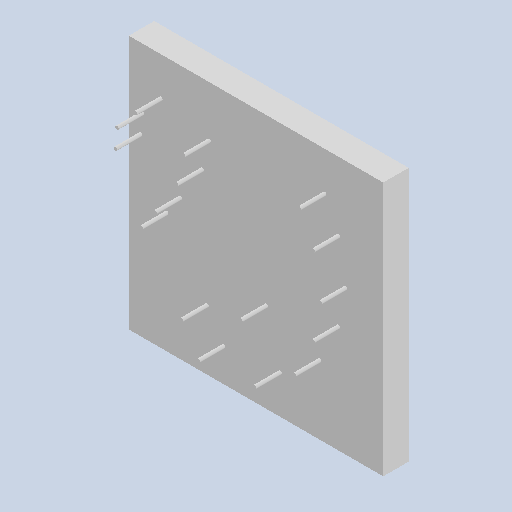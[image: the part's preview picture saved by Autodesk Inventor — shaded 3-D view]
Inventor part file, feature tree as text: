
AUTODESK INVENTOR PART (.ipt)
format: ipt  version: 2025 (Build 290162010, 162A)  size: 110,080 bytes
history: native  units: in
note: dims shown in document units (in); Inventor stores cm internally (conversion verified against a paired STEP export)
features: sketch x4, extrude x2
ambient origin geometry x8: Origin, YZ Plane, XZ Plane, XY Plane, X Axis, Y Axis, Z Axis, Center Point
bodies: Solid1 (feature_tree)
feature tree (6):
  extrude  "Extrusion1"  Depth=78.7402in
  extrude  "Extrusion2"  Depth=7.874in
  sketch  "Sketch Driven Pattern1"  dims[d0=78.7402in d1=78.7402in]
  sketch  "Sketch1"  dims[d2=7.874in d3=0.0in d4=1.063in]
  sketch  "Sketch2"  dims[d5=7.874in d6=0.0in]
  sketch  "Sketch3"
